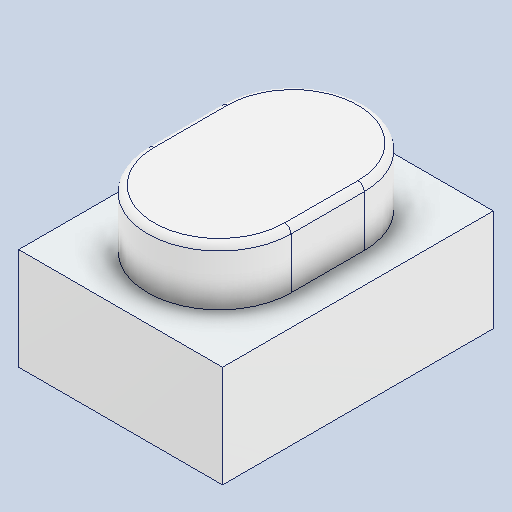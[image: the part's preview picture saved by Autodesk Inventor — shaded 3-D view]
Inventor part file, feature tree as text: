
AUTODESK INVENTOR PART (.ipt)
format: ipt  version: 2022.1 (Build 261234000, 234)  size: 124,416 bytes
history: imported  units: mm
features: imported_body x1
ambient origin geometry x8: Origin, YZ Plane, XZ Plane, XY Plane, X Axis, Y Axis, Z Axis, Center Point
bodies: Solid1 (imported_parasolid)
feature tree (1):
  imported_body  NMx_Import_Brep_tag  [imported B-rep: ~15 faces, bbox_mm=[3.2, 2.5, 4.25]]
